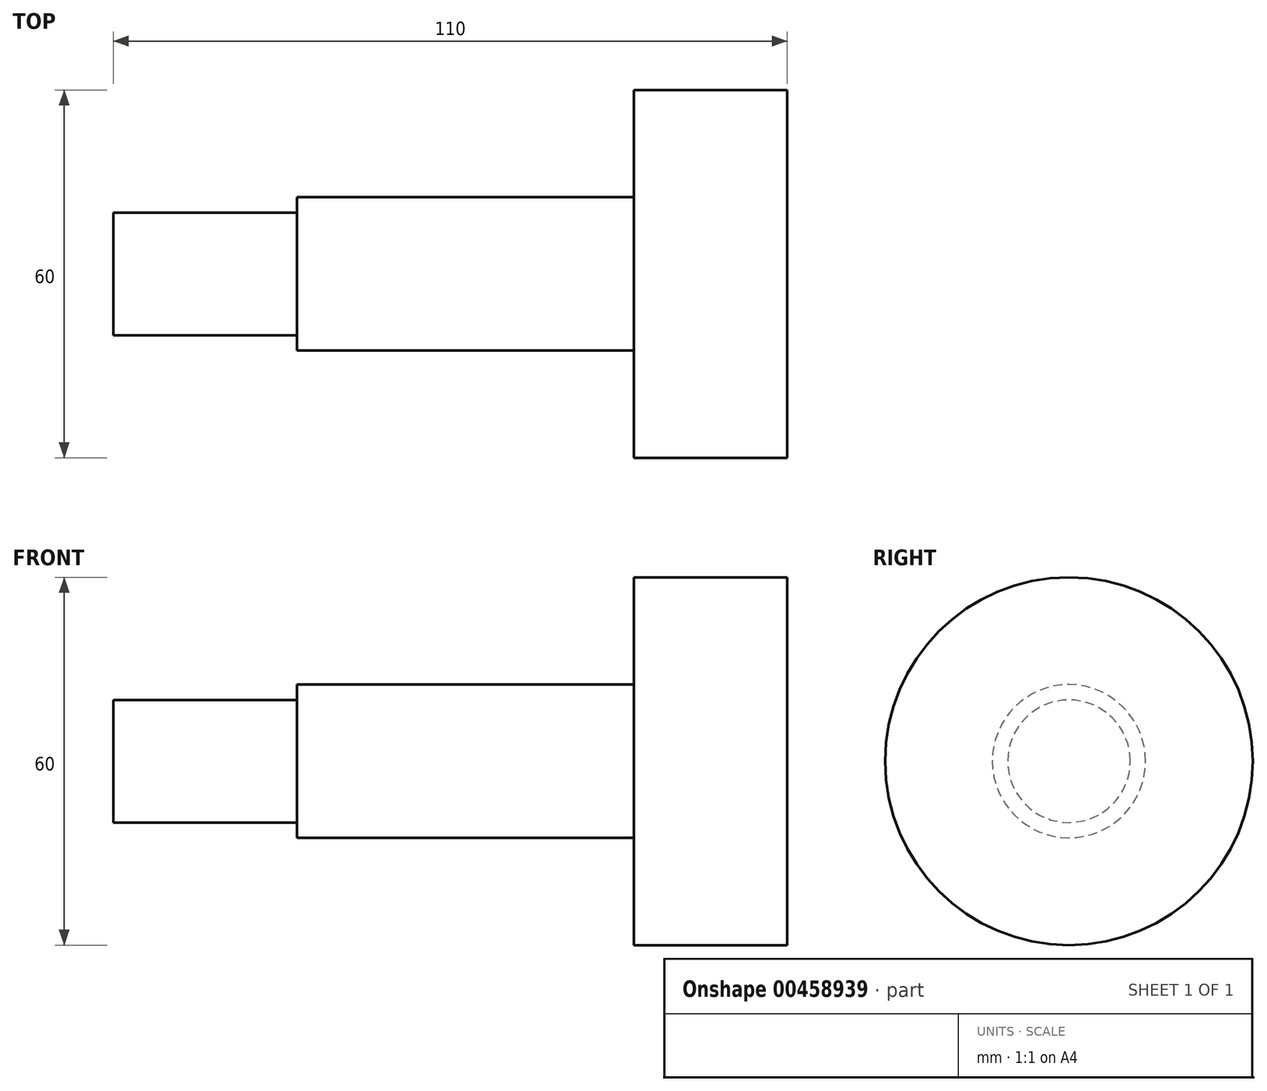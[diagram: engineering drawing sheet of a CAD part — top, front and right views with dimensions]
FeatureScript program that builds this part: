
annotation { "Feature Type Name" : "Feature", "Feature Type Description" : "" }
export const myFeature = defineFeature(function(context is Context, id is Id, definition is map)
    precondition{}
    {
        {
            var Q0;
            Q0=qCreatedBy(makeId("Top.planeOp"),FACE);
            var sketch = newSketch(context, id + "F0", { "sketchPlane" : qUnion([Q0])});
            skLineSegment(sketch, "E0", {"start": v(-85, 10) * mm, "end": v(-55, 10) * mm});
            skLineSegment(sketch, "E1", {"start": v(-55, 12.5) * mm, "end": v(-55, 10) * mm});
            skLineSegment(sketch, "E2", {"start": v(-55, 12.5) * mm, "end": v(0, 12.5) * mm});
            skLineSegment(sketch, "E3", {"start": v(0, 12.5) * mm, "end": v(0, 30) * mm});
            skLineSegment(sketch, "E4", {"start": v(0, 30) * mm, "end": v(25, 30) * mm});
            skLineSegment(sketch, "E5", {"start": v(25, 30) * mm, "end": v(25, 0) * mm});
            skLineSegment(sketch, "E6", {"start": v(25, 0) * mm, "end": v(-85, 0) * mm});
            skLineSegment(sketch, "E7", {"start": v(-85, 0) * mm, "end": v(-85, 10) * mm});
            skSolve(sketch);
        }
        {
            var Q0;
            Q0 = qSketchRegion(id + "F0", true);
            var Q1;
            Q1=sQuery(id+"F0.wireOp",EDGE,"E6");
            revolve(context, id + "F1", {"entities" : qUnion([Q0]), "axis" : qUnion([Q1]), "revolveType" : RevolveType.FULL});
        }
    });
